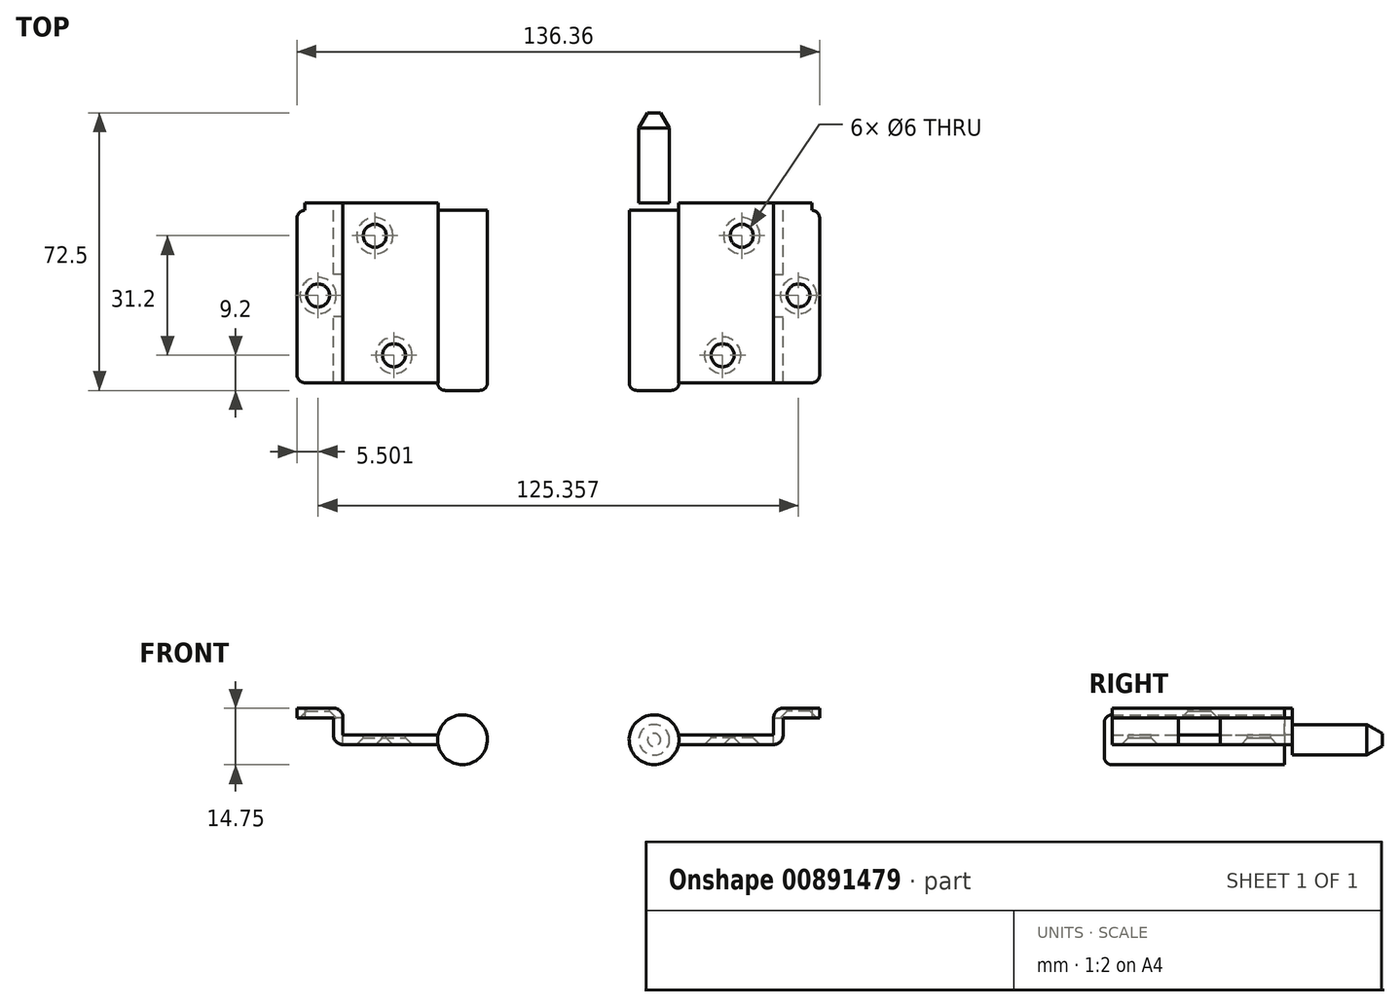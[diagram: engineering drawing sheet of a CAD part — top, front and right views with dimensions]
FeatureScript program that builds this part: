
annotation { "Feature Type Name" : "Feature", "Feature Type Description" : "" }
export const myFeature = defineFeature(function(context is Context, id is Id, definition is map)
    precondition{}
    {
        {
            var Q0;
            Q0=qCreatedBy(makeId("Front.planeOp"),FACE);
            var sketch = newSketch(context, id + "F0", { "sketchPlane" : qUnion([Q0])});
            skArc(sketch, "E0", {"start": v(6.38, 1.25) * mm, "mid": v(-6.5, 0) * mm, "end": v(6.38, -1.25) * mm});
            skLineSegment(sketch, "E1", {"start": v(6.38, 1.25) * mm, "end": v(31.18, 1.25) * mm});
            skLineSegment(sketch, "E2", {"start": v(31.18, 8.25) * mm, "end": v(43.18, 8.25) * mm});
            skLineSegment(sketch, "E3", {"start": v(43.18, 8.25) * mm, "end": v(43.18, 5.75) * mm});
            skLineSegment(sketch, "E4", {"start": v(43.18, 5.75) * mm, "end": v(33.68, 5.75) * mm});
            skLineSegment(sketch, "E5", {"start": v(33.68, -1.25) * mm, "end": v(6.38, -1.25) * mm});
            skLineSegment(sketch, "E6", {"start": v(33.68, 5.75) * mm, "end": v(33.68, -1.25) * mm});
            skLineSegment(sketch, "E7", {"start": v(31.18, 8.25) * mm, "end": v(31.18, 1.25) * mm});
            skSolve(sketch);
        }
        {
            var Q0;
            Q0=makeQuery(id+"F0.imprint","IMPRINT",FACE,{"disambiguationData":[TD([[makeQuery(id+"F0.imprint","IMPRINT",EDGE,{"derivedFrom":sQuery(id+"F0.wireOp",EDGE,"E0")}),1.0]])]});
            extrude(context, id + "F1", {"entities" : qUnion([Q0]), "depth" : 45 * mm, "offsetDistance" : 25 * mm});
        }
        {
            var Q0;
            Q0=makeQuery(id+"F1.opExtrude","CAP_EDGE",EDGE,{"disambiguationData":[OSD([sQuery(id+"F0.wireOp",EDGE,"E3")])],"isStart":false});
            var Q1;
            Q1=makeQuery(id+"F1.opExtrude","CAP_EDGE",EDGE,{"disambiguationData":[OSD([sQuery(id+"F0.wireOp",EDGE,"E3")])],"isStart":true});
            fillet(context, id + "F2", {"entities" : qUnion([Q0, Q1]), "radius" : 2 * mm, "tangentPropagation" : true, "allowEdgeOverflow" : false});
        }
        {
            var Q0;
            Q0=makeQuery(id+"F1.opExtrude","SWEPT_EDGE",EDGE,{"disambiguationData":[OSD([sQuery(id+"F0.wireOp",EDGE,"E5"),sQuery(id+"F0.wireOp",EDGE,"E6")])]});
            var Q1;
            Q1=makeQuery(id+"F1.opExtrude","SWEPT_EDGE",EDGE,{"disambiguationData":[OSD([sQuery(id+"F0.wireOp",EDGE,"E2"),sQuery(id+"F0.wireOp",EDGE,"E7")])]});
            fillet(context, id + "F3", {"entities" : qUnion([Q0, Q1]), "radius" : 2.5 * mm, "tangentPropagation" : true, "allowEdgeOverflow" : false});
        }
        {
            var Q0;
            Q0=makeQuery(id+"F1.opExtrude","CAP_FACE",FACE,{"disambiguationData":[OSD([sQuery(id+"F0.wireOp",EDGE,"E0"),sQuery(id+"F0.wireOp",EDGE,"E1"),sQuery(id+"F0.wireOp",EDGE,"WSlHtf5i-U6j4-Ynl4-FoHb-XjoWY4hGSOt6"),sQuery(id+"F0.wireOp",EDGE,"E2"),sQuery(id+"F0.wireOp",EDGE,"E3"),sQuery(id+"F0.wireOp",EDGE,"E4"),sQuery(id+"F0.wireOp",EDGE,"E5"),sQuery(id+"F0.wireOp",EDGE,"dJLKLTg6-jbDR-ftkV-erEf-zidkdKnkohMK"),sQuery(id+"F0.wireOp",EDGE,"M6QVCp6i-pHj4-OTcd-NfKp-MZP8uRFXvbLj"),sQuery(id+"F0.wireOp",EDGE,"RtBS60rh-hvOl-1zH0-KM05-FjQfmGGDyUj7")])],"isStart":true});
            var sketch = newSketch(context, id + "F4", { "sketchPlane" : qUnion([Q0])});
            skCircle(sketch, "E8", {"center": v(0, 0) * mm, "radius": 6.5 * mm});
            skSolve(sketch);
        }
        {
            var Q0;
            {var subQ0=sQuery(id+"F4.wireOp",EDGE,"E8");Q0=makeQuery(id+"F4.imprint","IMPRINT",FACE,{"disambiguationData":[TD([[makeQuery(id+"F4.imprint","IMPRINT",EDGE,{"disambiguationData":[OD(0.0)],"derivedFrom":subQ0}),-1.0]])]});}
            extrude(context, id + "F5", {"entities" : qUnion([Q0]), "operationType" : NewBodyOperationType.ADD, "depth" : 2 * mm, "offsetDistance" : 25 * mm});
        }
        {
            var Q0;
            Q0=makeQuery(id+"F5.opExtrude","CAP_FACE",FACE,{"disambiguationData":[OSD([sQuery(id+"F4.wireOp",EDGE,"E8")])],"isStart":false});
            var sketch = newSketch(context, id + "F6", { "sketchPlane" : qUnion([Q0])});
            skCircle(sketch, "E9", {"center": v(0, 0) * mm, "radius": 4 * mm});
            skSolve(sketch);
        }
        {
            var Q0;
            Q0=makeQuery(id+"F6.imprint","IMPRINT",FACE,{"disambiguationData":[TD([[makeQuery(id+"F6.imprint","IMPRINT",EDGE,{"derivedFrom":sQuery(id+"F6.wireOp",EDGE,"E9")}),1.0]])]});
            extrude(context, id + "F7", {"entities" : qUnion([Q0]), "operationType" : NewBodyOperationType.ADD, "depth" : 23.5 * mm, "offsetDistance" : 25 * mm});
        }
        {
            var Q0;
            Q0=makeQuery(id+"F7.opExtrude","CAP_EDGE",EDGE,{"disambiguationData":[OSD([sQuery(id+"F6.wireOp",EDGE,"E9")])],"isStart":false});
            chamfer(context, id + "F8", {"entities" : qUnion([Q0]), "chamferType" : ChamferType.TWO_OFFSETS, "width1" : 4 * mm, "oppositeDirection" : true, "width2" : 2.31 * mm, "tangentPropagation" : true});
        }
        {
            var Q0;
            Q0=makeQuery(id+"F1.opExtrude","SWEPT_FACE",FACE,{"disambiguationData":[OSD([sQuery(id+"F0.wireOp",EDGE,"E5")])]});
            var sketch = newSketch(context, id + "F9", { "sketchPlane" : qUnion([Q0])});
            skPoint(sketch, "E10", {"position": v(22.88, 6.6) * mm});
            skPoint(sketch, "E11", {"position": v(17.88, 37.8) * mm});
            skSolve(sketch);
        }
        {
            var Q0;
            Q0=sQuery(id+"F9.wireOp",VERTEX,"E10");
            var Q1;
            Q1=sQuery(id+"F9.wireOp",VERTEX,"E11");
            var Q2;
            Q2=sQuery(id+"F1gnd5VNBVrkXNz_1.wireOp",VERTEX,"af38a646-69fc-4794-a32b-26258d2a7c5d");
            var Q3;
            Q3=makeQuery(id+"F1.opExtrude","SWEPT_BODY",BODY,{"disambiguationData":[OSD([sQuery(id+"F0.wireOp",EDGE,"E0"),sQuery(id+"F0.wireOp",EDGE,"E1"),sQuery(id+"F0.wireOp",EDGE,"WSlHtf5i-U6j4-Ynl4-FoHb-XjoWY4hGSOt6"),sQuery(id+"F0.wireOp",EDGE,"E2"),sQuery(id+"F0.wireOp",EDGE,"E3"),sQuery(id+"F0.wireOp",EDGE,"E4"),sQuery(id+"F0.wireOp",EDGE,"E5"),sQuery(id+"F0.wireOp",EDGE,"dJLKLTg6-jbDR-ftkV-erEf-zidkdKnkohMK"),sQuery(id+"F0.wireOp",EDGE,"M6QVCp6i-pHj4-OTcd-NfKp-MZP8uRFXvbLj"),sQuery(id+"F0.wireOp",EDGE,"RtBS60rh-hvOl-1zH0-KM05-FjQfmGGDyUj7")])]});
            hole(context, id + "F10", {"style" : HoleStyle.C_SINK, "endStyle" : HoleEndStyle.THROUGH, "standardTappedOrClearance" : lookupTablePath({ "standard" : "ISO", "size" : "6", "type" : "Drilled" }), "standardBlindInLast" : lookupTablePath({ "standard" : "ISO", "size" : "6", "type" : "Drilled" }), "holeDiameter" : 6 * mm, "cSinkDiameter" : 9.5 * mm, "cSinkAngle" : 90 * degree, "majorDiameter" : 5 * mm, "isTappedThrough" : true, "tappedDepth" : 12 * mm, "tapClearance" : 3, "startFromSketch" : true, "locations" : qUnion([Q0, Q1, Q2]), "scope" : qUnion([Q3])});
        }
        {
            var Q0;
            Q0=makeQuery(id+"F1.opExtrude","CAP_FACE",FACE,{"disambiguationData":[OSD([sQuery(id+"F0.wireOp",EDGE,"E0"),sQuery(id+"F0.wireOp",EDGE,"E1"),sQuery(id+"F0.wireOp",EDGE,"WSlHtf5i-U6j4-Ynl4-FoHb-XjoWY4hGSOt6"),sQuery(id+"F0.wireOp",EDGE,"E2"),sQuery(id+"F0.wireOp",EDGE,"E3"),sQuery(id+"F0.wireOp",EDGE,"E4"),sQuery(id+"F0.wireOp",EDGE,"E5"),sQuery(id+"F0.wireOp",EDGE,"dJLKLTg6-jbDR-ftkV-erEf-zidkdKnkohMK"),sQuery(id+"F0.wireOp",EDGE,"M6QVCp6i-pHj4-OTcd-NfKp-MZP8uRFXvbLj"),sQuery(id+"F0.wireOp",EDGE,"RtBS60rh-hvOl-1zH0-KM05-FjQfmGGDyUj7")])],"isStart":false});
            var sketch = newSketch(context, id + "F11", { "sketchPlane" : qUnion([Q0])});
            skCircle(sketch, "E12", {"center": v(0, 0) * mm, "radius": 6.5 * mm});
            skSolve(sketch);
        }
        {
            var Q0;
            Q0=qSketchRegion(id+"F11",true);
            extrude(context, id + "F12", {"entities" : qUnion([Q0]), "operationType" : NewBodyOperationType.ADD, "depth" : 2 * mm, "offsetDistance" : 25 * mm});
        }
        {
            var Q0;
            Q0=makeQuery(id+"F12.opExtrude","CAP_EDGE",EDGE,{"disambiguationData":[OSD([sQuery(id+"F11.wireOp",EDGE,"E12")])],"isStart":false});
            fillet(context, id + "F13", {"entities" : qUnion([Q0]), "radius" : 2 * mm, "tangentPropagation" : true, "allowEdgeOverflow" : false});
        }
        {
            var Q0;
            Q0=makeQuery(id+"F1.opExtrude","SWEPT_FACE",FACE,{"disambiguationData":[OSD([sQuery(id+"F0.wireOp",EDGE,"E4")])]});
            var sketch = newSketch(context, id + "F14", { "sketchPlane" : qUnion([Q0])});
            skPoint(sketch, "E13", {"position": v(37.68, 22.2) * mm});
            skLineSegment(sketch, "E14.bottom", {"start": v(31.18, 27.7) * mm, "end": v(36.18, 27.7) * mm});
            skLineSegment(sketch, "E14.top", {"start": v(31.18, 16.7) * mm, "end": v(36.18, 16.7) * mm});
            skLineSegment(sketch, "E14.left", {"start": v(31.18, 27.7) * mm, "end": v(31.18, 16.7) * mm});
            skLineSegment(sketch, "E14.right", {"start": v(36.18, 27.7) * mm, "end": v(36.18, 16.7) * mm});
            skPoint(sketch, "E14.middle", {"position": v(33.68, 22.2) * mm});
            skPoint(sketch, "E14.middle.positionSnap0", {"position": v(33.68, 22.5) * mm});
            skPoint(sketch, "E14.centerSnap0", {"position": v(33.68, 22.5) * mm});
            skSolve(sketch);
        }
        {
            var Q0;
            Q0=qSketchRegion(id+"F14",true);
            extrude(context, id + "F15", {"entities" : qUnion([Q0]), "operationType" : NewBodyOperationType.REMOVE, "depth" : 25 * mm, "offsetDistance" : 25 * mm});
        }
        {
            var Q0;
            Q0=sQuery(id+"F14.wireOp",VERTEX,"E13");
            var Q1;
            Q1=makeQuery(id+"F1.opExtrude","SWEPT_BODY",BODY,{"disambiguationData":[OSD([sQuery(id+"F0.wireOp",EDGE,"E0"),sQuery(id+"F0.wireOp",EDGE,"E1"),sQuery(id+"F0.wireOp",EDGE,"E2"),sQuery(id+"F0.wireOp",EDGE,"E3"),sQuery(id+"F0.wireOp",EDGE,"E4"),sQuery(id+"F0.wireOp",EDGE,"E5"),sQuery(id+"F0.wireOp",EDGE,"E6"),sQuery(id+"F0.wireOp",EDGE,"E7")])]});
            hole(context, id + "F16", {"style" : HoleStyle.C_SINK, "endStyle" : HoleEndStyle.THROUGH, "standardTappedOrClearance" : lookupTablePath({ "standard" : "ISO", "size" : "6", "type" : "Drilled" }), "standardBlindInLast" : lookupTablePath({ "standard" : "ISO", "size" : "6", "type" : "Drilled" }), "holeDiameter" : 6 * mm, "cSinkDiameter" : 9.5 * mm, "cSinkAngle" : 90 * degree, "majorDiameter" : 5 * mm, "isTappedThrough" : true, "tappedDepth" : 12 * mm, "tapClearance" : 3, "startFromSketch" : true, "locations" : qUnion([Q0]), "scope" : qUnion([Q1])});
        }
        {
            var Q0;
            Q0=qCreatedBy(makeId("Right.planeOp"),FACE);
            cPlane(context, id + "F17", {"entities" : qUnion([Q0]), "cplaneType" : CPlaneType.OFFSET, "offset" : 25 * mm, "oppositeDirection" : true, "width" : 150 * mm, "height" : 150 * mm});
        }
        {
            var Q0;
            Q0=makeQuery(id+"F1.opExtrude","SWEPT_BODY",BODY,{"disambiguationData":[OSD([sQuery(id+"F0.wireOp",EDGE,"E0"),sQuery(id+"F0.wireOp",EDGE,"E1"),sQuery(id+"F0.wireOp",EDGE,"E2"),sQuery(id+"F0.wireOp",EDGE,"E3"),sQuery(id+"F0.wireOp",EDGE,"E4"),sQuery(id+"F0.wireOp",EDGE,"E5"),sQuery(id+"F0.wireOp",EDGE,"E6"),sQuery(id+"F0.wireOp",EDGE,"E7")])]});
            var Q1;
            Q1=qCreatedBy(id+"F17.planeOp",FACE);
            mirror(context, id + "F18", {"entities" : qUnion([Q0]), "mirrorPlane" : qUnion([Q1])});
        }
    });
